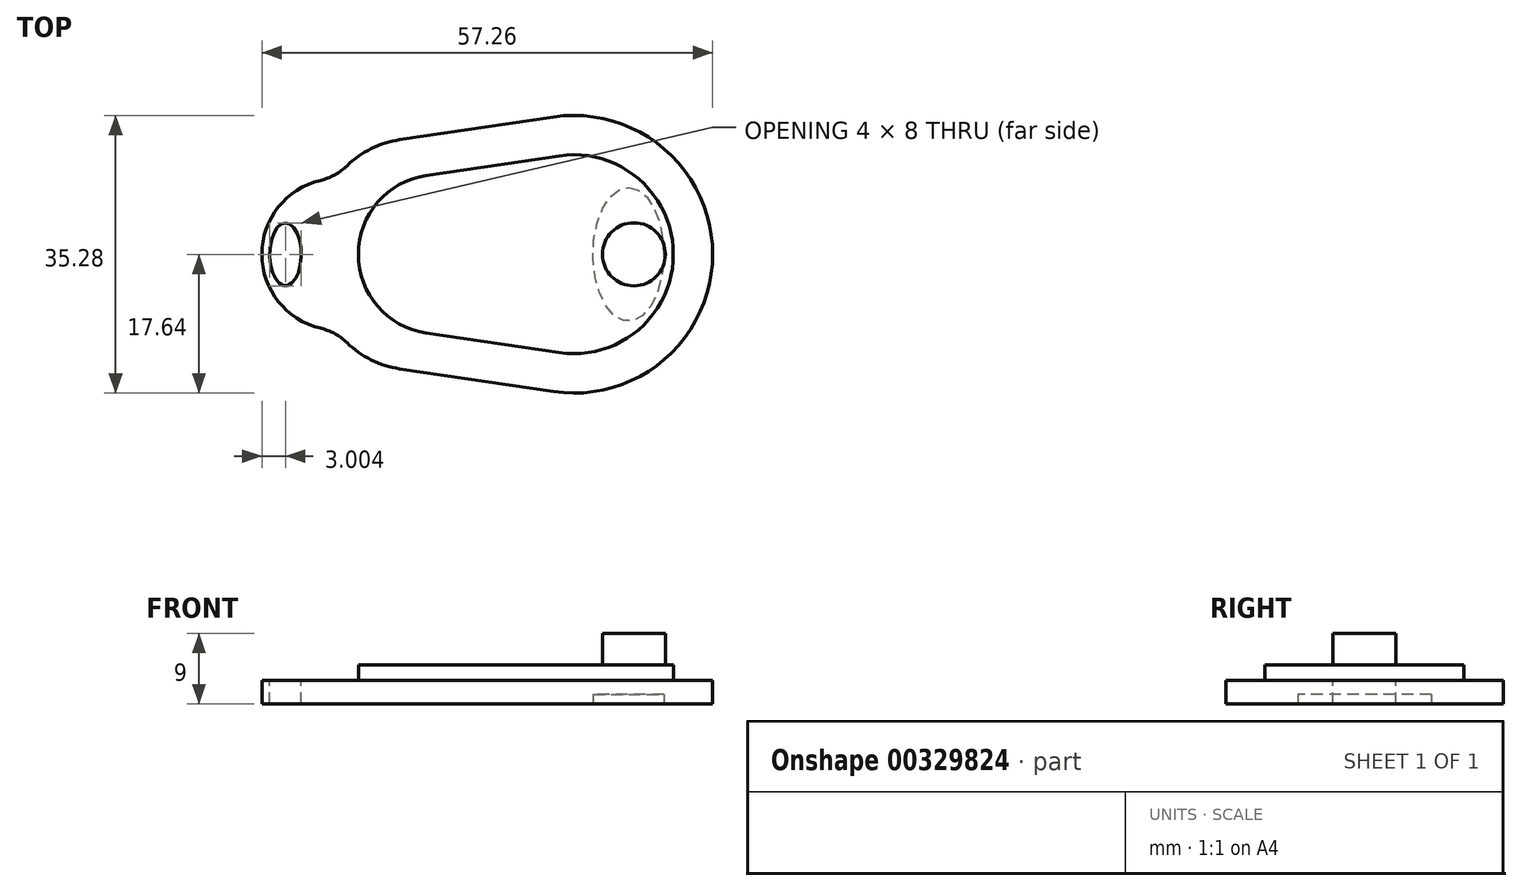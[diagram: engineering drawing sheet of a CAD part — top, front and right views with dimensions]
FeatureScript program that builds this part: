
annotation { "Feature Type Name" : "Feature", "Feature Type Description" : "" }
export const myFeature = defineFeature(function(context is Context, id is Id, definition is map)
    precondition{}
    {
        {
            var Q0;
            Q0=qCreatedBy(makeId("Top.planeOp"),FACE);
            var sketch = newSketch(context, id + "F0", { "sketchPlane" : qUnion([Q0])});
            skArc(sketch, "E0", {"start": v(-1.48, 10) * mm, "mid": v(-10.1, 0) * mm, "end": v(-1.48, -10) * mm});
            skLineSegment(sketch, "E1", {"start": v(-1.48, 10) * mm, "end": v(15.4, 12.5) * mm});
            skLineSegment(sketch, "E2", {"start": v(-1.48, -10) * mm, "end": v(15.4, -12.5) * mm});
            skArc(sketch, "E3", {"start": v(15.4, 12.5) * mm, "mid": v(29.9, 0) * mm, "end": v(15.4, -12.5) * mm});
            skSolve(sketch);
        }
        {
            var Q0;
            Q0=makeQuery(id+"F0.imprint","IMPRINT",FACE,{"disambiguationData":[TD([[makeQuery(id+"F0.imprint","IMPRINT",EDGE,{"derivedFrom":sQuery(id+"F0.wireOp",EDGE,"E0")}),1.0]])]});
            extrude(context, id + "F1", {"entities" : qUnion([Q0]), "depth" : 2 * mm});
        }
        {
            var Q0;
            Q0=makeQuery(id+"F1.opExtrude","CAP_FACE",FACE,{"disambiguationData":[OSD([sQuery(id+"F0.wireOp",EDGE,"E0"),sQuery(id+"F0.wireOp",EDGE,"E1"),sQuery(id+"F0.wireOp",EDGE,"E2"),sQuery(id+"F0.wireOp",EDGE,"E3")])],"isStart":false});
            var sketch = newSketch(context, id + "F2", { "sketchPlane" : qUnion([Q0])});
            skCircle(sketch, "E4", {"center": v(24.9, 0) * mm, "radius": 4 * mm});
            skSolve(sketch);
        }
        {
            var Q0;
            Q0 = qSketchRegion(id + "F2", true);
            extrude(context, id + "F3", {"entities" : qUnion([Q0]), "operationType" : NewBodyOperationType.ADD, "depth" : 4 * mm});
        }
        {
            var Q0;
            Q0=qCreatedBy(makeId("Top.planeOp"),FACE);
            var sketch = newSketch(context, id + "F4", { "sketchPlane" : qUnion([Q0])});
            skLineSegment(sketch, "E5.0", {"start": v(-4.85, -14.56) * mm, "end": v(14.67, -17.45) * mm});
            skArc(sketch, "E5.1", {"start": v(14.67, 17.45) * mm, "mid": v(34.9, 0) * mm, "end": v(14.67, -17.45) * mm});
            skLineSegment(sketch, "E5.2", {"start": v(-4.85, 14.56) * mm, "end": v(14.67, 17.45) * mm});
            skArc(sketch, "E6", {"start": v(-4.85, 14.56) * mm, "mid": v(-8.47, 13.42) * mm, "end": v(-11.56, 11.23) * mm});
            skArc(sketch, "E7", {"start": v(-14.93, 9.39) * mm, "mid": v(-13.12, 10.08) * mm, "end": v(-11.56, 11.23) * mm});
            skArc(sketch, "E8", {"start": v(-14.93, 9.39) * mm, "mid": v(-20.28, 5.99) * mm, "end": v(-22.37, 0) * mm});
            skArc(sketch, "E9.MirrorCS", {"start": v(-14.93, -9.39) * mm, "mid": v(-20.28, -5.99) * mm, "end": v(-22.37, 0) * mm});
            skArc(sketch, "E10.MirrorCS", {"start": v(-14.93, -9.39) * mm, "mid": v(-13.12, -10.08) * mm, "end": v(-11.56, -11.23) * mm});
            skArc(sketch, "E11.MirrorCS", {"start": v(-4.85, -14.56) * mm, "mid": v(-8.47, -13.42) * mm, "end": v(-11.56, -11.23) * mm});
            skEllipse(sketch, "E12", {"center": v(-19.37, 0) * mm, "majorRadius": 4 * mm, "minorRadius": 2 * mm, "majorAxis": v(0, 1)});
            skSolve(sketch);
        }
        {
            var Q0;
            Q0 = qSketchRegion(id + "F4", true);
            extrude(context, id + "F5", {"entities" : qUnion([Q0]), "oppositeDirection" : true, "depth" : 3 * mm});
        }
        {
            var Q0;
            Q0=makeQuery(id+"F5.opExtrude","CAP_FACE",FACE,{"disambiguationData":[OSD([sQuery(id+"F4.wireOp",EDGE,"E5.0"),sQuery(id+"F4.wireOp",EDGE,"E5.1"),sQuery(id+"F4.wireOp",EDGE,"E5.2"),sQuery(id+"F4.wireOp",EDGE,"E6"),sQuery(id+"F4.wireOp",EDGE,"E7"),sQuery(id+"F4.wireOp",EDGE,"E8"),sQuery(id+"F4.wireOp",EDGE,"E9.MirrorCS"),sQuery(id+"F4.wireOp",EDGE,"E10.MirrorCS"),sQuery(id+"F4.wireOp",EDGE,"E11.MirrorCS"),sQuery(id+"F4.wireOp",EDGE,"E12")])],"isStart":false});
            var sketch = newSketch(context, id + "F6", { "sketchPlane" : qUnion([Q0])});
            skEllipse(sketch, "E13", {"center": v(24.2, 0) * mm, "majorRadius": 8.5 * mm, "minorRadius": 4.5 * mm, "majorAxis": v(0, -1)});
            skFitSpline(sketch, "E14.0", {"points": [v(23.6, -7.63) * mm, v(24.2, -7.74) * mm, v(24.78, -7.63) * mm, v(25.42, -7.27) * mm, v(26.08, -6.62) * mm, v(26.68, -5.68) * mm, v(27.2, -4.5) * mm, v(27.6, -3.1) * mm, v(27.84, -1.59) * mm, v(27.92, 0) * mm, v(27.84, 1.59) * mm, v(27.6, 3.1) * mm, v(27.2, 4.5) * mm, v(26.68, 5.68) * mm, v(26.08, 6.62) * mm, v(25.42, 7.27) * mm, v(24.78, 7.63) * mm, v(24.2, 7.74) * mm, v(23.6, 7.63) * mm, v(22.97, 7.27) * mm, v(22.31, 6.62) * mm, v(21.7, 5.68) * mm, v(21.19, 4.5) * mm, v(20.8, 3.1) * mm, v(20.55, 1.59) * mm, v(20.47, 0) * mm, v(20.55, -1.59) * mm, v(20.8, -3.1) * mm, v(21.19, -4.5) * mm, v(21.7, -5.68) * mm, v(22.31, -6.62) * mm, v(22.97, -7.27) * mm, v(23.6, -7.63) * mm, v(24.2, -7.74) * mm, v(24.78, -7.63) * mm]});
            skEllipticalArc(sketch, "E15", {});
            skFitSpline(sketch, "E16.0", {"points": [v(27.09, -0.04) * mm, v(27.1, 0) * mm, v(27.09, 0.04) * mm, v(27.02, 0.17) * mm, v(26.81, 0.37) * mm, v(26.47, 0.58) * mm, v(26.01, 0.77) * mm, v(25.46, 0.91) * mm, v(24.84, 1) * mm, v(24.2, 1.04) * mm, v(23.55, 1) * mm, v(22.93, 0.91) * mm, v(22.38, 0.77) * mm, v(21.92, 0.58) * mm, v(21.58, 0.37) * mm, v(21.37, 0.17) * mm, v(21.3, 0.04) * mm, v(21.3, 0) * mm, v(21.3, -0.04) * mm, v(21.37, -0.17) * mm, v(21.58, -0.37) * mm, v(21.92, -0.58) * mm, v(22.38, -0.77) * mm, v(22.93, -0.91) * mm, v(23.55, -1) * mm, v(24.2, -1.04) * mm, v(24.84, -1) * mm, v(25.46, -0.91) * mm, v(26.01, -0.77) * mm, v(26.47, -0.58) * mm, v(26.81, -0.37) * mm, v(27.02, -0.17) * mm, v(27.09, -0.04) * mm, v(27.1, 0) * mm, v(27.09, 0.04) * mm]});
            skArc(sketch, "E17", {"start": v(26.68, 5.62) * mm, "mid": v(25.55, 3.81) * mm, "end": v(24.87, 1.8) * mm});
            skArc(sketch, "E18", {"start": v(27.06, 4.8) * mm, "mid": v(26.2, 3.3) * mm, "end": v(25.67, 1.68) * mm});
            skArc(sketch, "E19.trimOffspring", {"start": v(25.54, 0.88) * mm, "mid": v(25.5, 0) * mm, "end": v(25.54, -0.88) * mm});
            skArc(sketch, "E20.trimOffspring", {"start": v(24.75, 1) * mm, "mid": v(24.7, 0) * mm, "end": v(24.75, -1) * mm});
            skFitSpline(sketch, "E21.trimOffspring", {"points": [v(27.09, -0.04) * mm, v(27.1, 0) * mm, v(27.09, 0.04) * mm, v(27.02, 0.17) * mm, v(26.81, 0.37) * mm, v(26.47, 0.58) * mm, v(26.01, 0.77) * mm, v(25.46, 0.91) * mm, v(24.84, 1) * mm, v(24.2, 1.04) * mm, v(23.55, 1) * mm, v(22.93, 0.91) * mm, v(22.38, 0.77) * mm, v(21.92, 0.58) * mm, v(21.58, 0.37) * mm, v(21.37, 0.17) * mm, v(21.3, 0.04) * mm, v(21.3, 0) * mm, v(21.3, -0.04) * mm, v(21.37, -0.17) * mm, v(21.58, -0.37) * mm, v(21.92, -0.58) * mm, v(22.38, -0.77) * mm, v(22.93, -0.91) * mm, v(23.55, -1) * mm, v(24.2, -1.04) * mm, v(24.84, -1) * mm, v(25.46, -0.91) * mm, v(26.01, -0.77) * mm, v(26.47, -0.58) * mm, v(26.81, -0.37) * mm, v(27.02, -0.17) * mm, v(27.09, -0.04) * mm, v(27.1, 0) * mm, v(27.09, 0.04) * mm]});
            skEllipticalArc(sketch, "E22.trimOffspring", {});
            skArc(sketch, "E23.trimOffspring", {"start": v(25.67, -1.68) * mm, "mid": v(26.2, -3.3) * mm, "end": v(27.06, -4.8) * mm});
            skArc(sketch, "E24.trimOffspring", {"start": v(24.87, -1.8) * mm, "mid": v(25.55, -3.81) * mm, "end": v(26.68, -5.62) * mm});
            skFitSpline(sketch, "E25.trimOffspring", {"points": [v(23.6, -7.63) * mm, v(24.2, -7.74) * mm, v(24.78, -7.63) * mm, v(25.42, -7.27) * mm, v(26.08, -6.62) * mm, v(26.68, -5.68) * mm, v(27.2, -4.5) * mm, v(27.6, -3.1) * mm, v(27.84, -1.59) * mm, v(27.92, 0) * mm, v(27.84, 1.59) * mm, v(27.6, 3.1) * mm, v(27.2, 4.5) * mm, v(26.68, 5.68) * mm, v(26.08, 6.62) * mm, v(25.42, 7.27) * mm, v(24.78, 7.63) * mm, v(24.2, 7.74) * mm, v(23.6, 7.63) * mm, v(22.97, 7.27) * mm, v(22.31, 6.62) * mm, v(21.7, 5.68) * mm, v(21.19, 4.5) * mm, v(20.8, 3.1) * mm, v(20.55, 1.59) * mm, v(20.47, 0) * mm, v(20.55, -1.59) * mm, v(20.8, -3.1) * mm, v(21.19, -4.5) * mm, v(21.7, -5.68) * mm, v(22.31, -6.62) * mm, v(22.97, -7.27) * mm, v(23.6, -7.63) * mm, v(24.2, -7.74) * mm, v(24.78, -7.63) * mm]});
            const initialGuessF6  = {"E15": [0.02419430762529373, 0, 1, 0, 0.003695, 0.0018265818611021404, 1.385668778978517, 4.897516528201069], "E22.trimOffspring": [0.02419430762529373, 0, 1, 0, 0.003695, 0.0018265818611021404, 5.122221799587564, 1.1609635075920217]};
            skSetInitialGuess(sketch, initialGuessF6);
            skSolve(sketch);
        }
        {
            var Q0;
            Q0 = qSketchRegion(id + "F6", true);
            extrude(context, id + "F7", {"entities" : qUnion([Q0]), "operationType" : NewBodyOperationType.REMOVE, "oppositeDirection" : true, "depth" : 1.2 * mm});
        }
    });
